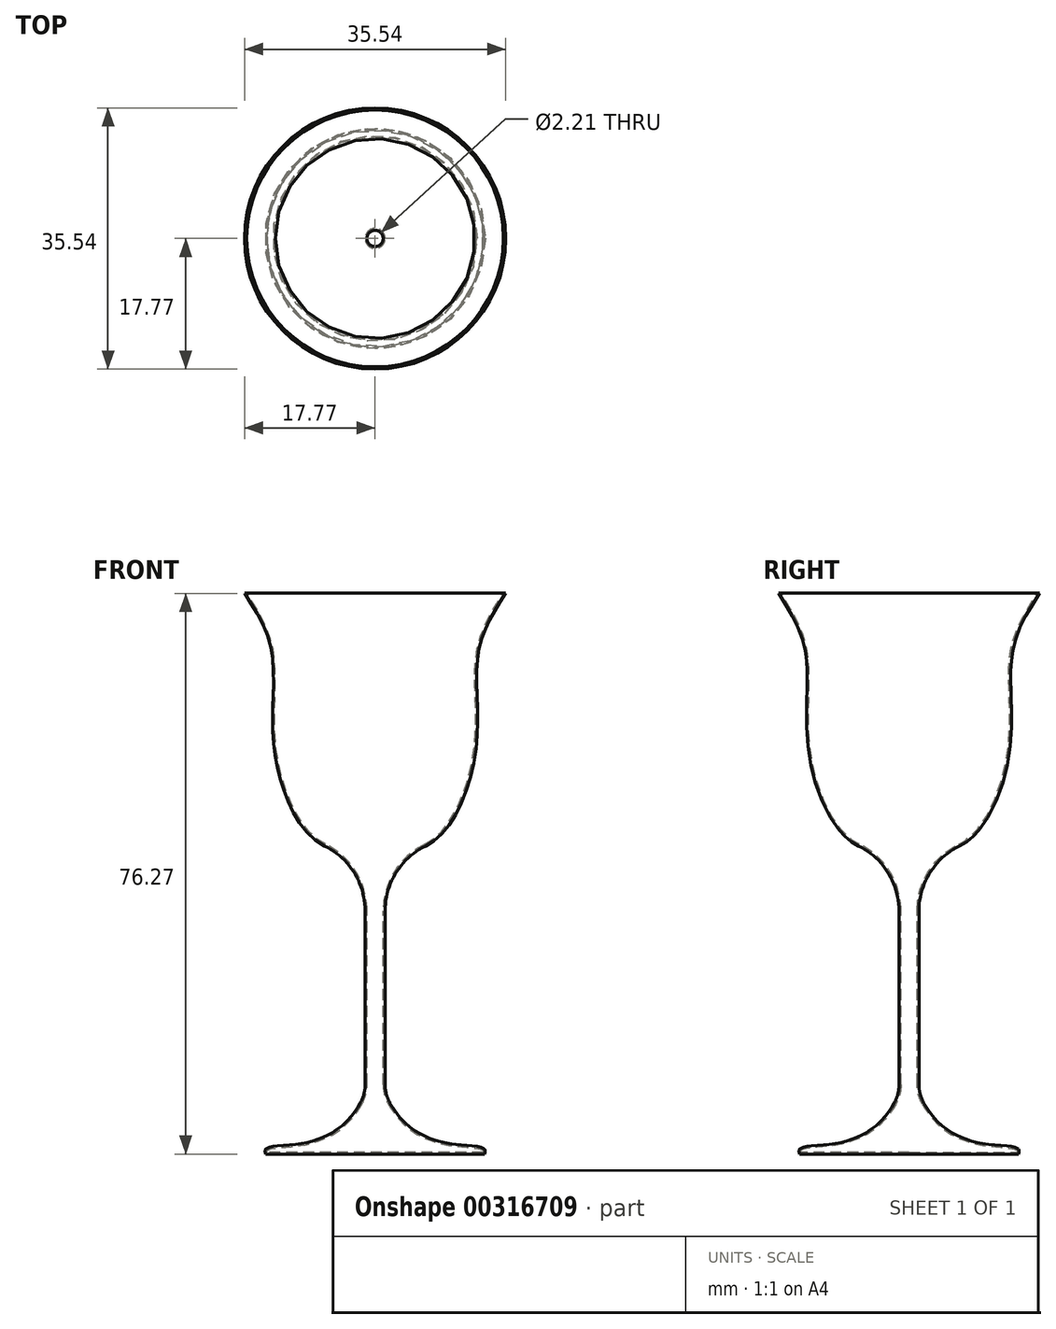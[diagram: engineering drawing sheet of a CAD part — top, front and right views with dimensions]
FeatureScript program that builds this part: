
annotation { "Feature Type Name" : "Feature", "Feature Type Description" : "" }
export const myFeature = defineFeature(function(context is Context, id is Id, definition is map)
    precondition{}
    {
        {
            var Q0;
            Q0=qCreatedBy(makeId("Front.planeOp"),FACE);
            var sketch = newSketch(context, id + "F0", { "sketchPlane" : qUnion([Q0])});
            skLineSegment(sketch, "E0", {"start": v(0, 0) * mm, "end": v(0, 76) * mm, "construction": true});
            skLineSegment(sketch, "E1", {"start": v(0, 0) * mm, "end": v(-14.9, 0) * mm, "construction": true});
            skLineSegment(sketch, "E2", {"start": v(-14.9, 0) * mm, "end": v(0, 0) * mm});
            skFitSpline(sketch, "E3", {"points": [v(-14.9, 0) * mm, v(-14.9, 0.68) * mm, v(-11.28, 1.27) * mm, v(-7.52, 2.12) * mm, v(-1.36, 8.22) * mm], "startDerivative": vector(-2.55, 7.36) * mm, "endDerivative": vector(14.82, 31.85) * mm});
            skLineSegment(sketch, "E4", {"start": v(-1.36, 8.22) * mm, "end": v(-1.36, 40.76) * mm});
            skFitSpline(sketch, "E5", {"points": [v(-1.36, 40.76) * mm, v(-8.43, 42.92) * mm, v(-13.76, 55.43) * mm, v(-14.1, 68.43) * mm, v(-17.77, 76.27) * mm], "startDerivative": vector(-36.23, 2.85) * mm, "endDerivative": vector(-20.67, 32.06) * mm});
            skLineSegment(sketch, "E6", {"start": v(-17.77, 76.27) * mm, "end": v(0, 76) * mm});
            skLineSegment(sketch, "E7", {"start": v(0, 76) * mm, "end": v(0, 0) * mm});
            skSolve(sketch);
        }
        {
            var Q0;
            Q0=makeQuery(id+"F0.imprint","IMPRINT",FACE,{"disambiguationData":[TD([[makeQuery(id+"F0.imprint","IMPRINT",EDGE,{"derivedFrom":sQuery(id+"F0.wireOp",EDGE,"E2")}),1.0]])]});
            var Q1;
            Q1=sQuery(id+"F0.wireOp",EDGE,"E7");
            revolve(context, id + "F1", {"entities" : qUnion([Q0]), "axis" : qUnion([Q1]), "revolveType" : RevolveType.FULL});
        }
        {
            var Q0;
            Q0=makeQuery(id+"F1.opRevolve","SWEPT_EDGE",EDGE,{"disambiguationData":[OSD([sQuery(id+"F0.wireOp",EDGE,"E4"),sQuery(id+"F0.wireOp",EDGE,"E5")])]});
            fillet(context, id + "F2", {"entities" : qUnion([Q0]), "radius" : 9.83 * mm, "tangentPropagation" : true, "allowEdgeOverflow" : false});
        }
        {
            var Q0;
            Q0=makeQuery(id+"F1.opRevolve","SWEPT_EDGE",EDGE,{"disambiguationData":[OSD([sQuery(id+"F0.wireOp",EDGE,"E3"),sQuery(id+"F0.wireOp",EDGE,"E4")])]});
            fillet(context, id + "F3", {"entities" : qUnion([Q0]), "radius" : 5.08 * mm, "tangentPropagation" : true, "allowEdgeOverflow" : false});
        }
        {
            var Q0;
            Q0=makeQuery(id+"F1.opRevolve","SWEPT_FACE",FACE,{"disambiguationData":[OSD([sQuery(id+"F0.wireOp",EDGE,"E6")])]});
            shell(context, id + "F4", {"entities" : qUnion([Q0]), "thickness" : 0.25 * mm});
        }
    });
